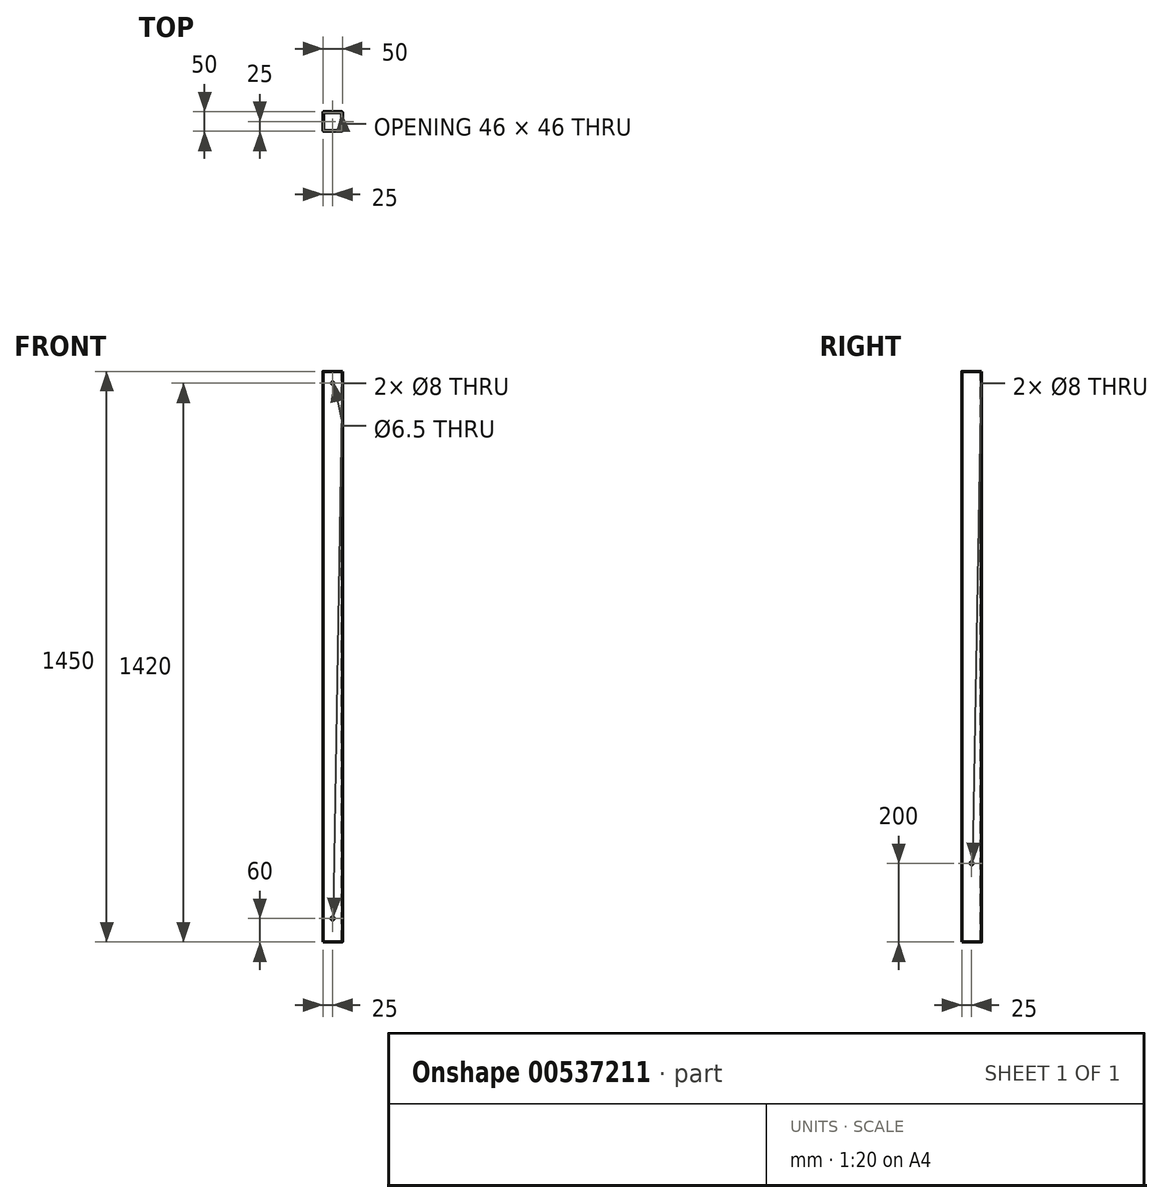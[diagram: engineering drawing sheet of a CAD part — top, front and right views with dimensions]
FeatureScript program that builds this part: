
annotation { "Feature Type Name" : "Feature", "Feature Type Description" : "" }
export const myFeature = defineFeature(function(context is Context, id is Id, definition is map)
    precondition{}
    {
        {
            var Q0;
            Q0=qCreatedBy(makeId("Top.planeOp"),FACE);
            var sketch = newSketch(context, id + "F0", { "sketchPlane" : qUnion([Q0])});
            skLineSegment(sketch, "E0.bottom", {"start": v(-22, -25) * mm, "end": v(22, -25) * mm});
            skLineSegment(sketch, "E0.top", {"start": v(-22, 25) * mm, "end": v(22, 25) * mm});
            skLineSegment(sketch, "E0.left", {"start": v(-25, -22) * mm, "end": v(-25, 22) * mm});
            skLineSegment(sketch, "E0.right", {"start": v(25, -22) * mm, "end": v(25, 22) * mm});
            skPoint(sketch, "E1.visualSharp", {"position": v(-25, 25) * mm});
            skArc(sketch, "E1.filletArc", {"start": v(-22, 25) * mm, "mid": v(-24.12, 24.12) * mm, "end": v(-25, 22) * mm});
            skPoint(sketch, "E2.visualSharp", {"position": v(25, 25) * mm});
            skArc(sketch, "E2.filletArc", {"start": v(25, 22) * mm, "mid": v(24.12, 24.12) * mm, "end": v(22, 25) * mm});
            skPoint(sketch, "E3.visualSharp", {"position": v(25, -25) * mm});
            skArc(sketch, "E3.filletArc", {"start": v(22, -25) * mm, "mid": v(24.12, -24.12) * mm, "end": v(25, -22) * mm});
            skPoint(sketch, "E4.visualSharp", {"position": v(-25, -25) * mm});
            skArc(sketch, "E4.filletArc", {"start": v(-25, -22) * mm, "mid": v(-24.12, -24.12) * mm, "end": v(-22, -25) * mm});
            skSolve(sketch);
        }
        {
            var Q0;
            Q0 = qSketchRegion(id + "F0", true);
            extrude(context, id + "F1", {"entities" : qUnion([Q0]), "depth" : 1450 * mm, "offsetDistance" : 25 * mm});
        }
        {
            var Q0;
            Q0=makeQuery(id+"F1.opExtrude","CAP_FACE",FACE,{"disambiguationData":[OSD([sQuery(id+"F0.wireOp",EDGE,"E0.bottom"),sQuery(id+"F0.wireOp",EDGE,"E0.top"),sQuery(id+"F0.wireOp",EDGE,"E0.left"),sQuery(id+"F0.wireOp",EDGE,"E0.right"),sQuery(id+"F0.wireOp",EDGE,"E1.filletArc"),sQuery(id+"F0.wireOp",EDGE,"E2.filletArc"),sQuery(id+"F0.wireOp",EDGE,"E3.filletArc"),sQuery(id+"F0.wireOp",EDGE,"E4.filletArc")])],"isStart":false});
            var Q1;
            Q1=makeQuery(id+"F1.opExtrude","CAP_FACE",FACE,{"disambiguationData":[OSD([sQuery(id+"F0.wireOp",EDGE,"E0.bottom"),sQuery(id+"F0.wireOp",EDGE,"E0.top"),sQuery(id+"F0.wireOp",EDGE,"E0.left"),sQuery(id+"F0.wireOp",EDGE,"E0.right"),sQuery(id+"F0.wireOp",EDGE,"E1.filletArc"),sQuery(id+"F0.wireOp",EDGE,"E2.filletArc"),sQuery(id+"F0.wireOp",EDGE,"E3.filletArc"),sQuery(id+"F0.wireOp",EDGE,"E4.filletArc")])],"isStart":true});
            shell(context, id + "F2", {"entities" : qUnion([Q0, Q1]), "thickness" : 2 * mm});
        }
        {
            var Q0;
            Q0=makeQuery(id+"F1.opExtrude","SWEPT_FACE",FACE,{"disambiguationData":[OSD([sQuery(id+"F0.wireOp",EDGE,"E0.bottom")])]});
            var sketch = newSketch(context, id + "F3", { "sketchPlane" : qUnion([Q0])});
            skPoint(sketch, "E5", {"position": v(0, 1420) * mm});
            skSolve(sketch);
        }
        {
            var Q0;
            Q0=sQuery(id+"F3.wireOp",VERTEX,"E5");
            var Q1;
            Q1=makeQuery(id+"F1.opExtrude","SWEPT_BODY",BODY,{"disambiguationData":[OSD([sQuery(id+"F0.wireOp",EDGE,"E0.bottom"),sQuery(id+"F0.wireOp",EDGE,"E0.top"),sQuery(id+"F0.wireOp",EDGE,"E0.left"),sQuery(id+"F0.wireOp",EDGE,"E0.right"),sQuery(id+"F0.wireOp",EDGE,"E1.filletArc"),sQuery(id+"F0.wireOp",EDGE,"E2.filletArc"),sQuery(id+"F0.wireOp",EDGE,"E3.filletArc"),sQuery(id+"F0.wireOp",EDGE,"E4.filletArc")])]});
            hole(context, id + "F4", {"style" : HoleStyle.SIMPLE, "endStyle" : HoleEndStyle.BLIND, "holeDiameter" : 6.5 * mm, "holeDepth" : 25 * mm, "isTappedThrough" : true, "tappedDepth" : 12 * mm, "tapClearance" : 3, "locations" : qUnion([Q0]), "scope" : qUnion([Q1])});
        }
        {
            var Q0;
            Q0=makeQuery(id+"F1.opExtrude","SWEPT_FACE",FACE,{"disambiguationData":[OSD([sQuery(id+"F0.wireOp",EDGE,"E0.bottom")])]});
            var sketch = newSketch(context, id + "F5", { "sketchPlane" : qUnion([Q0])});
            skPoint(sketch, "E6", {"position": v(0, 60) * mm});
            skSolve(sketch);
        }
        {
            var Q0;
            Q0=sQuery(id+"F5.wireOp",VERTEX,"E6");
            var Q1;
            Q1=makeQuery(id+"F1.opExtrude","SWEPT_BODY",BODY,{"disambiguationData":[OSD([sQuery(id+"F0.wireOp",EDGE,"E0.bottom"),sQuery(id+"F0.wireOp",EDGE,"E0.top"),sQuery(id+"F0.wireOp",EDGE,"E0.left"),sQuery(id+"F0.wireOp",EDGE,"E0.right"),sQuery(id+"F0.wireOp",EDGE,"E1.filletArc"),sQuery(id+"F0.wireOp",EDGE,"E2.filletArc"),sQuery(id+"F0.wireOp",EDGE,"E3.filletArc"),sQuery(id+"F0.wireOp",EDGE,"E4.filletArc")])]});
            hole(context, id + "F6", {"style" : HoleStyle.SIMPLE, "endStyle" : HoleEndStyle.THROUGH, "holeDiameter" : 8 * mm, "isTappedThrough" : true, "tappedDepth" : 12 * mm, "tapClearance" : 3, "locations" : qUnion([Q0]), "scope" : qUnion([Q1])});
        }
        {
            var Q0;
            Q0=makeQuery(id+"F1.opExtrude","SWEPT_FACE",FACE,{"disambiguationData":[OSD([sQuery(id+"F0.wireOp",EDGE,"E0.left")])]});
            var sketch = newSketch(context, id + "F7", { "sketchPlane" : qUnion([Q0])});
            skPoint(sketch, "E7", {"position": v(0, 200) * mm});
            skSolve(sketch);
        }
        {
            var Q0;
            Q0=sQuery(id+"F7.wireOp",VERTEX,"E7");
            var Q1;
            Q1=makeQuery(id+"F1.opExtrude","SWEPT_BODY",BODY,{"disambiguationData":[OSD([sQuery(id+"F0.wireOp",EDGE,"E0.bottom"),sQuery(id+"F0.wireOp",EDGE,"E0.top"),sQuery(id+"F0.wireOp",EDGE,"E0.left"),sQuery(id+"F0.wireOp",EDGE,"E0.right"),sQuery(id+"F0.wireOp",EDGE,"E1.filletArc"),sQuery(id+"F0.wireOp",EDGE,"E2.filletArc"),sQuery(id+"F0.wireOp",EDGE,"E3.filletArc"),sQuery(id+"F0.wireOp",EDGE,"E4.filletArc")])]});
            hole(context, id + "F8", {"style" : HoleStyle.SIMPLE, "endStyle" : HoleEndStyle.THROUGH, "holeDiameter" : 8 * mm, "isTappedThrough" : true, "tappedDepth" : 12 * mm, "tapClearance" : 3, "locations" : qUnion([Q0]), "scope" : qUnion([Q1])});
        }
    });
